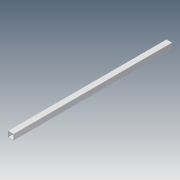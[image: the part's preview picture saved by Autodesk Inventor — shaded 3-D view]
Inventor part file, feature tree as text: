
AUTODESK INVENTOR PART (.ipt)
format: ipt  version: 2014 (Build 180170000, 170)  size: 90,112 bytes
history: native  units: in
note: dims shown in document units (in); Inventor stores cm internally (conversion verified against a paired STEP export)
features: extrude x1, sketch x1
ambient origin geometry x8: Origin, YZ Plane, XZ Plane, XY Plane, X Axis, Y Axis, Z Axis, Center Point
bodies: Solid1 (feature_tree)
feature tree (2):
  extrude  "Extrusion1"  Depth=1.0in
  sketch  "Sketch1"  dims[d0=1.0in d1=1.0in d2=0.07in d3=0.063in d4=27.5in d5=0.0in]
